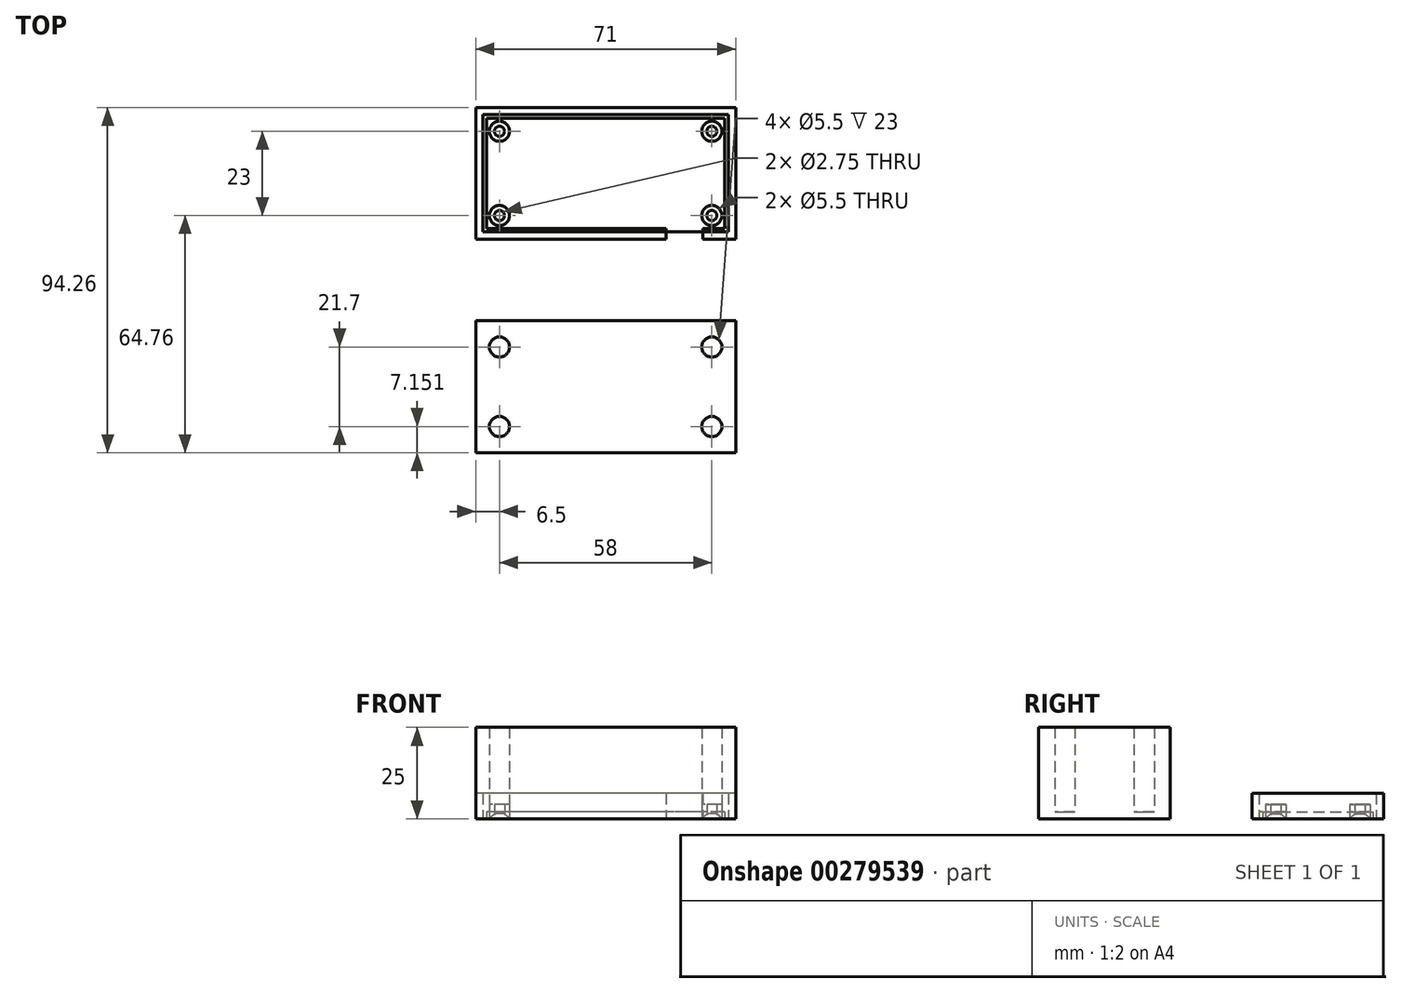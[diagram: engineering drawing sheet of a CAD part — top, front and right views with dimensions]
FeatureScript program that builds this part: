
annotation { "Feature Type Name" : "Feature", "Feature Type Description" : "" }
export const myFeature = defineFeature(function(context is Context, id is Id, definition is map)
    precondition{}
    {
        {
            var Q0;
            Q0=qCreatedBy(makeId("Top.planeOp"),FACE);
            var sketch = newSketch(context, id + "F0", { "sketchPlane" : qUnion([Q0])});
            skLineSegment(sketch, "E0.bottom", {"start": v(32.5, -15) * mm, "end": v(-32.5, -15) * mm});
            skLineSegment(sketch, "E0.top", {"start": v(32.5, 15) * mm, "end": v(-32.5, 15) * mm});
            skLineSegment(sketch, "E0.left", {"start": v(32.5, -15) * mm, "end": v(32.5, 15) * mm});
            skLineSegment(sketch, "E0.right", {"start": v(-32.5, -15) * mm, "end": v(-32.5, 15) * mm});
            skPoint(sketch, "E0.middle", {"position": v(0, 0) * mm});
            skCircle(sketch, "E1", {"center": v(29, 11.5) * mm, "radius": 1.38 * mm});
            skLineSegment(sketch, "E2", {"start": v(29, 15) * mm, "end": v(29, 11.5) * mm, "construction": true});
            skLineSegment(sketch, "E3", {"start": v(29, 11.5) * mm, "end": v(32.5, 11.5) * mm, "construction": true});
            skCircle(sketch, "E4.MirrorC", {"center": v(29, -11.5) * mm, "radius": 1.38 * mm});
            skCircle(sketch, "E5.MirrorC", {"center": v(-29, 11.5) * mm, "radius": 1.38 * mm});
            skCircle(sketch, "E6.MirrorC", {"center": v(-29, -11.5) * mm, "radius": 1.38 * mm});
            skLineSegment(sketch, "E7.0", {"start": v(33.5, 16) * mm, "end": v(-33.5, 16) * mm});
            skLineSegment(sketch, "E7.1", {"start": v(33.5, -16) * mm, "end": v(33.5, 16) * mm});
            skLineSegment(sketch, "E7.2", {"start": v(33.5, -16) * mm, "end": v(-33.5, -16) * mm});
            skLineSegment(sketch, "E7.3", {"start": v(-33.5, -16) * mm, "end": v(-33.5, 16) * mm});
            skLineSegment(sketch, "E8.0", {"start": v(35.5, 18) * mm, "end": v(-35.5, 18) * mm});
            skLineSegment(sketch, "E8.1", {"start": v(35.5, -18) * mm, "end": v(35.5, 18) * mm});
            skLineSegment(sketch, "E8.2", {"start": v(35.5, -18) * mm, "end": v(-35.5, -18) * mm});
            skLineSegment(sketch, "E8.3", {"start": v(-35.5, -18) * mm, "end": v(-35.5, 18) * mm});
            skLineSegment(sketch, "E9", {"start": v(-32.5, -15) * mm, "end": v(21.5, -15) * mm});
            skLineSegment(sketch, "E10.bottom", {"start": v(16.5, -15) * mm, "end": v(26.5, -15) * mm});
            skLineSegment(sketch, "E10.top", {"start": v(16.5, -18) * mm, "end": v(26.5, -18) * mm});
            skLineSegment(sketch, "E10.left", {"start": v(16.5, -15) * mm, "end": v(16.5, -18) * mm});
            skLineSegment(sketch, "E10.right", {"start": v(26.5, -15) * mm, "end": v(26.5, -18) * mm});
            skCircle(sketch, "E11", {"center": v(29, 11.5) * mm, "radius": 2.75 * mm});
            skCircle(sketch, "E12.MirrorC", {"center": v(29, -11.5) * mm, "radius": 2.75 * mm});
            skCircle(sketch, "E13.MirrorC", {"center": v(-29, 11.5) * mm, "radius": 2.75 * mm});
            skCircle(sketch, "E14.MirrorC", {"center": v(-29, -11.5) * mm, "radius": 2.75 * mm});
            skSolve(sketch);
        }
        {
            var Q0;
            {var subQ5=sQuery(id+"F0.wireOp",EDGE,"E10.top");Q0=makeQuery(id+"F0.imprint","IMPRINT",FACE,{"disambiguationData":[TD([[makeQuery(id+"F0.imprint","IMPRINT",EDGE,{"derivedFrom":subQ5}),1.0]])]});}
            var Q1;
            {var subQ3=sQuery(id+"F0.wireOp",EDGE,"E0.bottom");Q1=makeQuery(id+"F0.imprint","IMPRINT",FACE,{"disambiguationData":[TD([[makeQuery(id+"F0.imprint","IMPRINT",EDGE,{"derivedFrom":subQ3}),-1.0]])]});}
            var Q2;
            Q2=makeQuery(id+"F0.imprint","IMPRINT",FACE,{"disambiguationData":[TD([[makeQuery(id+"F0.imprint","IMPRINT",EDGE,{"derivedFrom":sQuery(id+"F0.wireOp",EDGE,"E7.0")}),-1.0]])]});
            var Q3;
            {var subQ5=sQuery(id+"F0.wireOp",EDGE,"E0.bottom");Q3=makeQuery(id+"F0.imprint","IMPRINT",FACE,{"disambiguationData":[TD([[makeQuery(id+"F0.imprint","IMPRINT",EDGE,{"derivedFrom":subQ5}),1.0]])]});}
            var Q4;
            Q4=makeQuery(id+"F0.imprint","IMPRINT",FACE,{"disambiguationData":[TD([[makeQuery(id+"F0.imprint","IMPRINT",EDGE,{"derivedFrom":sQuery(id+"F0.wireOp",EDGE,"E1")}),-1.0]])]});
            var Q5;
            Q5=makeQuery(id+"F0.imprint","IMPRINT",FACE,{"disambiguationData":[TD([[makeQuery(id+"F0.imprint","IMPRINT",EDGE,{"derivedFrom":sQuery(id+"F0.wireOp",EDGE,"E4.MirrorC")}),1.0]])]});
            var Q6;
            {var subQ3=sQuery(id+"F0.wireOp",EDGE,"E7.2");var subQ5=sQuery(id+"F0.wireOp",EDGE,"E10.right");var subQ8=makeQuery(id+"F0.imprint","INTERSECT",VERTEX,{"derivedFrom":[subQ3,subQ5]});Q6=makeQuery(id+"F0.imprint","IMPRINT",FACE,{"disambiguationData":[TD([[makeQuery(id+"F0.imprint","IMPRINT",EDGE,{"disambiguationData":[TD([[subQ8,-1.0]])],"derivedFrom":subQ3}),-1.0]])]});}
            var Q7;
            Q7=makeQuery(id+"F0.imprint","IMPRINT",FACE,{"disambiguationData":[TD([[makeQuery(id+"F0.imprint","IMPRINT",EDGE,{"derivedFrom":sQuery(id+"F0.wireOp",EDGE,"E5.MirrorC")}),1.0]])]});
            var Q8;
            Q8=makeQuery(id+"F0.imprint","IMPRINT",FACE,{"disambiguationData":[TD([[makeQuery(id+"F0.imprint","IMPRINT",EDGE,{"derivedFrom":sQuery(id+"F0.wireOp",EDGE,"E6.MirrorC")}),-1.0]])]});
            extrude(context, id + "F1", {"entities" : qUnion([Q0, Q1, Q2, Q3, Q4, Q5, Q6, Q7, Q8]), "depth" : 2 * mm});
        }
        {
            var Q0;
            Q0=makeQuery(id+"F0.imprint","IMPRINT",FACE,{"disambiguationData":[TD([[makeQuery(id+"F0.imprint","IMPRINT",EDGE,{"derivedFrom":sQuery(id+"F0.wireOp",EDGE,"E7.0")}),-1.0]])]});
            extrude(context, id + "F2", {"entities" : qUnion([Q0]), "operationType" : NewBodyOperationType.ADD, "depth" : 7 * mm});
        }
        {
            var Q0;
            Q0=makeQuery(id+"F0.imprint","IMPRINT",FACE,{"disambiguationData":[TD([[makeQuery(id+"F0.imprint","IMPRINT",EDGE,{"derivedFrom":sQuery(id+"F0.wireOp",EDGE,"E6.MirrorC")}),-1.0]])]});
            var Q1;
            Q1=makeQuery(id+"F0.imprint","IMPRINT",FACE,{"disambiguationData":[TD([[makeQuery(id+"F0.imprint","IMPRINT",EDGE,{"derivedFrom":sQuery(id+"F0.wireOp",EDGE,"E5.MirrorC")}),1.0]])]});
            var Q2;
            Q2=makeQuery(id+"F0.imprint","IMPRINT",FACE,{"disambiguationData":[TD([[makeQuery(id+"F0.imprint","IMPRINT",EDGE,{"derivedFrom":sQuery(id+"F0.wireOp",EDGE,"E4.MirrorC")}),1.0]])]});
            var Q3;
            Q3=makeQuery(id+"F0.imprint","IMPRINT",FACE,{"disambiguationData":[TD([[makeQuery(id+"F0.imprint","IMPRINT",EDGE,{"derivedFrom":sQuery(id+"F0.wireOp",EDGE,"E1")}),-1.0]])]});
            extrude(context, id + "F3", {"entities" : qUnion([Q0, Q1, Q2, Q3]), "operationType" : NewBodyOperationType.ADD, "depth" : 4 * mm});
        }
        {
            var Q0;
            Q0=makeQuery(id+"F1.opExtrude","CAP_EDGE",EDGE,{"disambiguationData":[OSD([sQuery(id+"F0.wireOp",EDGE,"E6.MirrorC")])],"isStart":true});
            var Q1;
            Q1=makeQuery(id+"F1.opExtrude","CAP_EDGE",EDGE,{"disambiguationData":[OSD([sQuery(id+"F0.wireOp",EDGE,"E5.MirrorC")])],"isStart":true});
            var Q2;
            Q2=makeQuery(id+"F1.opExtrude","CAP_EDGE",EDGE,{"disambiguationData":[OSD([sQuery(id+"F0.wireOp",EDGE,"E4.MirrorC")])],"isStart":true});
            var Q3;
            Q3=makeQuery(id+"F1.opExtrude","CAP_EDGE",EDGE,{"disambiguationData":[OSD([sQuery(id+"F0.wireOp",EDGE,"E1")])],"isStart":true});
            chamfer(context, id + "F4", {"entities" : qUnion([Q0, Q1, Q2, Q3]), "width" : 1.5 * mm, "tangentPropagation" : true});
        }
        {
            var Q0;
            Q0=qCreatedBy(makeId("Top.planeOp"),FACE);
            var sketch = newSketch(context, id + "F5", { "sketchPlane" : qUnion([Q0])});
            skLineSegment(sketch, "E15.bottom", {"start": v(-35.5, -76.26) * mm, "end": v(35.5, -76.26) * mm});
            skLineSegment(sketch, "E15.top", {"start": v(-35.5, -40.26) * mm, "end": v(35.5, -40.26) * mm});
            skLineSegment(sketch, "E15.left", {"start": v(-35.5, -76.26) * mm, "end": v(-35.5, -40.26) * mm});
            skLineSegment(sketch, "E15.right", {"start": v(35.5, -76.26) * mm, "end": v(35.5, -40.26) * mm});
            skPoint(sketch, "E15.middle", {"position": v(0, -58.26) * mm});
            skCircle(sketch, "E16", {"center": v(29, -47.4) * mm, "radius": 1.38 * mm});
            skLineSegment(sketch, "E17", {"start": v(29, -40.9) * mm, "end": v(29, -47.4) * mm, "construction": true});
            skLineSegment(sketch, "E18", {"start": v(29, -47.4) * mm, "end": v(35.5, -47.4) * mm, "construction": true});
            skCircle(sketch, "E19", {"center": v(29, -47.4) * mm, "radius": 2.75 * mm});
            skLineSegment(sketch, "E20", {"start": v(35.5, -58.26) * mm, "end": v(-35.5, -58.26) * mm});
            skCircle(sketch, "E21.MirrorC", {"center": v(-29, -47.4) * mm, "radius": 1.38 * mm});
            skCircle(sketch, "E22.MirrorC", {"center": v(-29, -47.4) * mm, "radius": 2.75 * mm});
            skCircle(sketch, "E23.MirrorC", {"center": v(29, -69.1) * mm, "radius": 1.38 * mm});
            skCircle(sketch, "E24.MirrorC", {"center": v(29, -69.1) * mm, "radius": 2.75 * mm});
            skCircle(sketch, "E25.MirrorC", {"center": v(-29, -69.1) * mm, "radius": 1.38 * mm});
            skCircle(sketch, "E26.MirrorC", {"center": v(-29, -69.1) * mm, "radius": 2.75 * mm});
            skSolve(sketch);
        }
        {
            var Q0;
            {var subQ2=sQuery(id+"F5.wireOp",EDGE,"E15.top");Q0=makeQuery(id+"F5.imprint","IMPRINT",FACE,{"disambiguationData":[TD([[makeQuery(id+"F5.imprint","IMPRINT",EDGE,{"derivedFrom":subQ2}),-1.0]])]});}
            var Q1;
            {var subQ2=sQuery(id+"F5.wireOp",EDGE,"E15.bottom");Q1=makeQuery(id+"F5.imprint","IMPRINT",FACE,{"disambiguationData":[TD([[makeQuery(id+"F5.imprint","IMPRINT",EDGE,{"derivedFrom":subQ2}),1.0]])]});}
            var Q2;
            Q2=makeQuery(id+"F5.imprint","IMPRINT",FACE,{"disambiguationData":[TD([[makeQuery(id+"F5.imprint","IMPRINT",EDGE,{"derivedFrom":sQuery(id+"F5.wireOp",EDGE,"E21.MirrorC")}),1.0]])]});
            var Q3;
            Q3=makeQuery(id+"F5.imprint","IMPRINT",FACE,{"disambiguationData":[TD([[makeQuery(id+"F5.imprint","IMPRINT",EDGE,{"derivedFrom":sQuery(id+"F5.wireOp",EDGE,"E21.MirrorC")}),-1.0]])]});
            var Q4;
            Q4=makeQuery(id+"F5.imprint","IMPRINT",FACE,{"disambiguationData":[TD([[makeQuery(id+"F5.imprint","IMPRINT",EDGE,{"derivedFrom":sQuery(id+"F5.wireOp",EDGE,"E16")}),-1.0]])]});
            var Q5;
            Q5=makeQuery(id+"F5.imprint","IMPRINT",FACE,{"disambiguationData":[TD([[makeQuery(id+"F5.imprint","IMPRINT",EDGE,{"derivedFrom":sQuery(id+"F5.wireOp",EDGE,"E16")}),1.0]])]});
            var Q6;
            Q6=makeQuery(id+"F5.imprint","IMPRINT",FACE,{"disambiguationData":[TD([[makeQuery(id+"F5.imprint","IMPRINT",EDGE,{"derivedFrom":sQuery(id+"F5.wireOp",EDGE,"E25.MirrorC")}),1.0]])]});
            var Q7;
            Q7=makeQuery(id+"F5.imprint","IMPRINT",FACE,{"disambiguationData":[TD([[makeQuery(id+"F5.imprint","IMPRINT",EDGE,{"derivedFrom":sQuery(id+"F5.wireOp",EDGE,"E25.MirrorC")}),-1.0]])]});
            var Q8;
            Q8=makeQuery(id+"F5.imprint","IMPRINT",FACE,{"disambiguationData":[TD([[makeQuery(id+"F5.imprint","IMPRINT",EDGE,{"derivedFrom":sQuery(id+"F5.wireOp",EDGE,"E23.MirrorC")}),1.0]])]});
            var Q9;
            Q9=makeQuery(id+"F5.imprint","IMPRINT",FACE,{"disambiguationData":[TD([[makeQuery(id+"F5.imprint","IMPRINT",EDGE,{"derivedFrom":sQuery(id+"F5.wireOp",EDGE,"E23.MirrorC")}),-1.0]])]});
            extrude(context, id + "F6", {"entities" : qUnion([Q0, Q1, Q2, Q3, Q4, Q5, Q6, Q7, Q8, Q9]), "depth" : 2 * mm});
        }
        {
            var Q0;
            Q0 = qSketchRegion(id + "F5", true);
            extrude(context, id + "F7", {"entities" : qUnion([Q0]), "operationType" : NewBodyOperationType.ADD, "depth" : 25 * mm});
        }
    });
